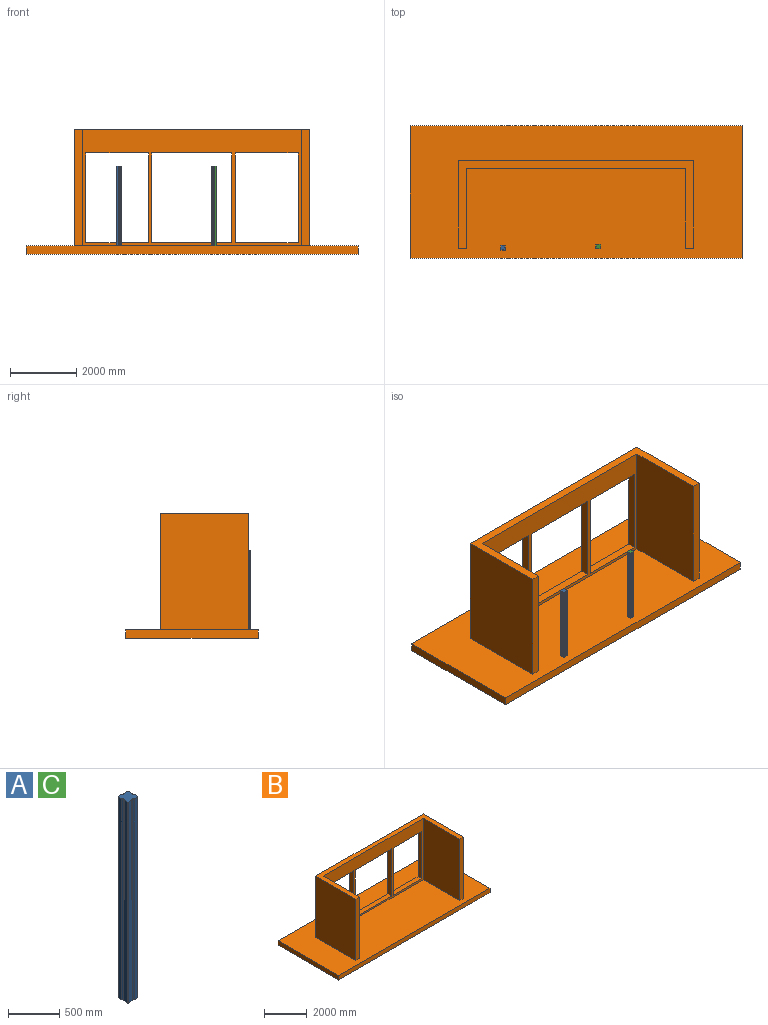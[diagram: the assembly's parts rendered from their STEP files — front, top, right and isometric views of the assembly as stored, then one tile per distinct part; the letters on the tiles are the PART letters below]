
ASSEMBLY  parts=3 mates=2
PART A: 26 faces, bbox 140x140x2400 mm
  f0: plane 2400x10mm, normal (1,0,0), area 24000mm2, adj f1,f23,f24,f25
  f1: cylinder r=10mm len=2400mm, axis (0,0,-1), area 37699.1mm2, adj f0,f2,f24,f25
  f2: plane 2400x45mm, normal (1,0,0), area 108000mm2, adj f1,f3,f24,f25
  f3: cylinder r=10mm len=2400mm, axis (0,0,-1), area 37699.1mm2, adj f2,f4,f24,f25
  f4: plane 2400x45mm, normal (0,1,0), area 108000mm2, adj f3,f5,f24,f25
  f5: cylinder r=10mm len=2400mm, axis (0,0,-1), area 37699.1mm2, adj f4,f6,f24,f25
  f6: plane 2400x10mm, normal (0,1,0), area 24000mm2, adj f5,f7,f24,f25
  f7: cylinder r=10mm len=2400mm, axis (0,0,-1), area 37699.1mm2, adj f6,f8,f24,f25
  f8: plane 2400x45mm, normal (0,1,0), area 108000mm2, adj f7,f9,f24,f25
  f9: cylinder r=10mm len=2400mm, axis (0,0,-1), area 37699.1mm2, adj f8,f10,f24,f25
  f10: plane 2400x45mm, normal (-1,0,0), area 108000mm2, adj f9,f11,f24,f25
  f11: cylinder r=10mm len=2400mm, axis (0,0,-1), area 37699.1mm2, adj f10,f12,f24,f25
  f12: plane 2400x10mm, normal (-1,0,0), area 24000mm2, adj f11,f13,f24,f25
  f13: cylinder r=10mm len=2400mm, axis (0,0,-1), area 37699.1mm2, adj f12,f14,f24,f25
  f14: plane 2400x45mm, normal (-1,0,0), area 108000mm2, adj f13,f15,f24,f25
  f15: cylinder r=10mm len=2400mm, axis (0,0,-1), area 37699.1mm2, adj f14,f16,f24,f25
  f16: plane 2400x45mm, normal (0,-1,0), area 108000mm2, adj f15,f17,f24,f25
  f17: cylinder r=10mm len=2400mm, axis (0,0,-1), area 37699.1mm2, adj f16,f18,f24,f25
  f18: plane 2400x10mm, normal (0,-1,0), area 24000mm2, adj f17,f19,f24,f25
  f19: cylinder r=10mm len=2400mm, axis (0,0,-1), area 37699.1mm2, adj f18,f20,f24,f25
  f20: plane 2400x45mm, normal (0,-1,0), area 108000mm2, adj f19,f21,f24,f25
  f21: cylinder r=10mm len=2400mm, axis (0,0,-1), area 37699.1mm2, adj f20,f22,f24,f25
  f22: plane 2400x45mm, normal (1,0,0), area 108000mm2, adj f21,f23,f24,f25
  f23: cylinder r=10mm len=2400mm, axis (0,0,-1), area 37699.1mm2, adj f0,f22,f24,f25
  f24: plane 140x140mm, normal (0,0,1), area 18942.5mm2, adj f0,f1,f2,f3,f4,f5,f6,f7
  f25: plane 140x140mm, normal (0,0,-1), area 18942.5mm2, adj f0,f1,f2,f3,f4,f5,f6,f7
PART B: 27 faces, bbox 10000x4000x3750 mm
  f0: plane 6600x3500mm, normal (0,-1,0), area 6360000mm2, adj f6,f9,f10,f14,f15,f16,f17,f18
  f1: plane 7100x3500mm, normal (0,1,0), area 8110000mm2, adj f6,f12,f13,f14,f15,f16,f17,f18
  f2: plane 4000x250mm, normal (-1,0,0), area 1000000mm2, adj f3,f5,f6,f7
  f3: plane 10000x250mm, normal (0,-1,0), area 2500000mm2, adj f2,f4,f6,f7
  f4: plane 4000x250mm, normal (1,0,0), area 1000000mm2, adj f3,f5,f6,f7
  f5: plane 10000x250mm, normal (0,1,0), area 2500000mm2, adj f2,f4,f6,f7
  f6: plane 10000x4000mm, normal (0,0,1), area 37025000mm2, adj f0,f1,f2,f3,f4,f5,f8,f9
  f7: plane 10000x4000mm, normal (0,0,-1), area 40000000mm2, adj f2,f3,f4,f5
  f8: plane 3500x250mm, normal (0,-1,0), area 875000mm2, adj f6,f9,f13,f14
  f9: plane 3500x2400mm, normal (1,0,0), area 8400000mm2, adj f0,f6,f8,f14
  f10: plane 3500x2400mm, normal (-1,0,0), area 8400000mm2, adj f0,f6,f11,f14
  f11: plane 3500x250mm, normal (0,-1,0), area 875000mm2, adj f6,f10,f12,f14
  f12: plane 3500x2650mm, normal (1,0,0), area 9275000mm2, adj f1,f6,f11,f14
  f13: plane 3500x2650mm, normal (-1,0,0), area 9275000mm2, adj f1,f6,f8,f14
  f14: plane 7100x2650mm, normal (0,0,1), area 2975000mm2, adj f0,f1,f8,f9,f10,f11,f12,f13
  f15: plane 2700x250mm, normal (1,0,0), area 675000mm2, adj f0,f1,f16,f18
  f16: plane 1894.29x250mm, normal (0,0,1), area 473573.4mm2, adj f0,f1,f15,f17
  f17: plane 2700x250mm, normal (-1,0,0), area 675000mm2, adj f0,f1,f16,f18
  f18: plane 1894.29x250mm, normal (0,0,-1), area 473573.4mm2, adj f0,f1,f15,f17
  f19: plane 2700x250mm, normal (1,0,0), area 675000mm2, adj f0,f1,f20,f22
  f20: plane 2411.41x250mm, normal (0,0,1), area 602853.3mm2, adj f0,f1,f19,f21
  f21: plane 2700x250mm, normal (-1,0,0), area 675000mm2, adj f0,f1,f20,f22
  f22: plane 2411.41x250mm, normal (0,0,-1), area 602853.3mm2, adj f0,f1,f19,f21
  f23: plane 2700x250mm, normal (1,0,0), area 675000mm2, adj f0,f1,f24,f26
  f24: plane 1894.29x250mm, normal (0,0,1), area 473573.4mm2, adj f0,f1,f23,f25
  f25: plane 2700x250mm, normal (-1,0,0), area 675000mm2, adj f0,f1,f24,f26
  f26: plane 1894.29x250mm, normal (0,0,-1), area 473573.4mm2, adj f0,f1,f23,f25
PART C: same geometry as A
PLACE A t=(207.6,-1589.15,-3731.85)mm
PLACE B t=(1270.06,-93.63,-3981.85)mm
PLACE C t=(3076.91,-1550.1,-3731.85)mm
MATE planar A.f25 <-> B.f6  axis (0,0,-1) through (277.6,-1519.15,-3731.85)mm
MATE planar B.f6 <-> C.f25  axis (0,0,1) through (2478.86,142.8,-3731.85)mm
